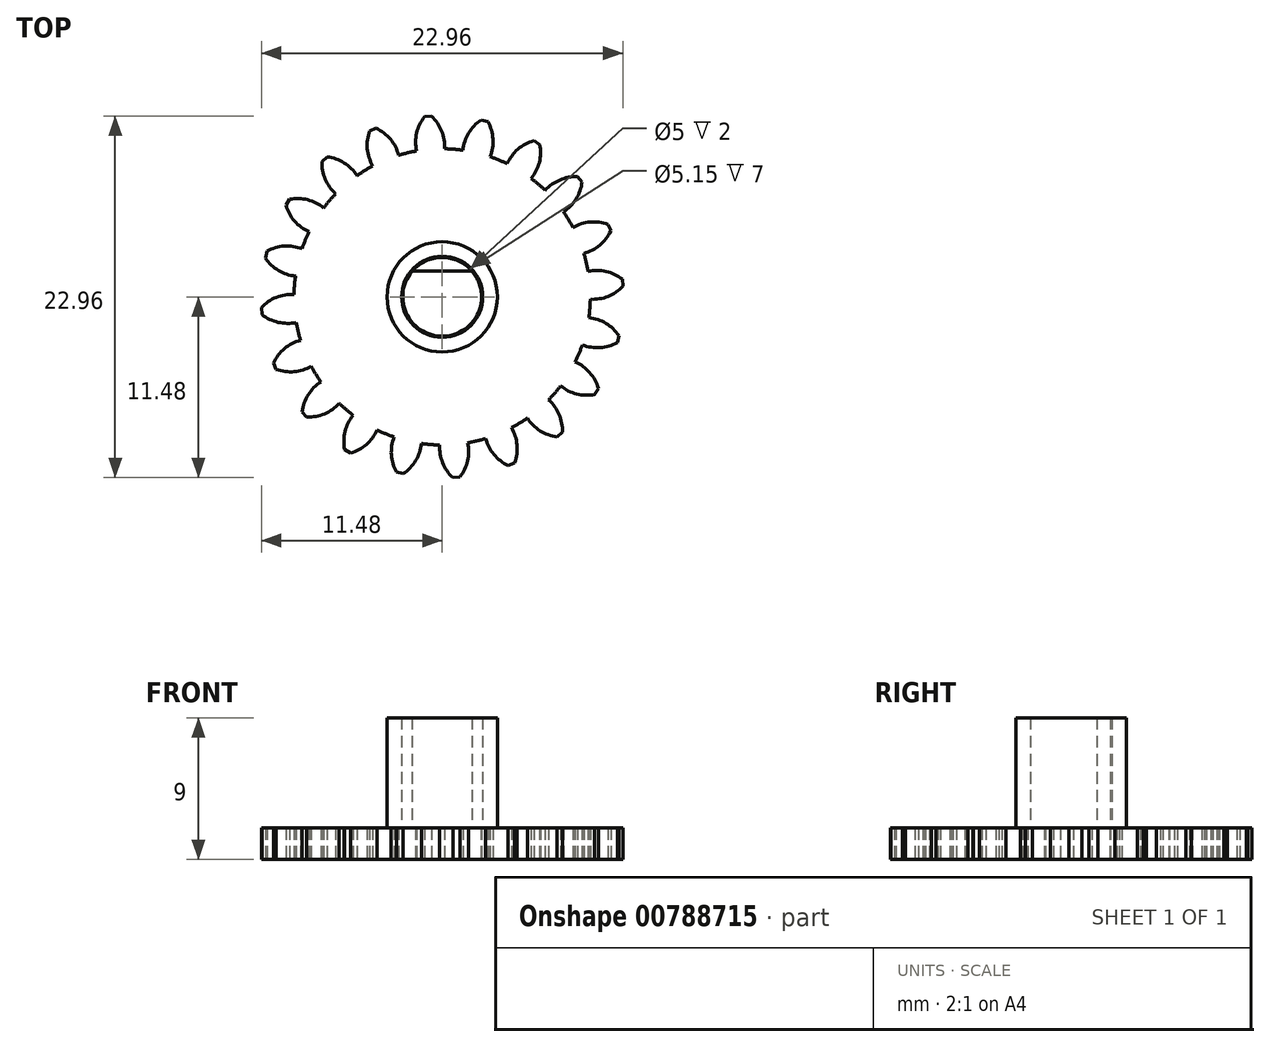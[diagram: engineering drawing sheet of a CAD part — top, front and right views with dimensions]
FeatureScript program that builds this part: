
annotation { "Feature Type Name" : "Feature", "Feature Type Description" : "" }
export const myFeature = defineFeature(function(context is Context, id is Id, definition is map)
    precondition{}
    {
        {
            assignVariable(context, id + "F0", {"name" : "GearDepth", "anyValue" : 2});
        }
        {
            var Q0;
            Q0=qCreatedBy(makeId("Top.planeOp"),FACE);
            var sketch = newSketch(context, id + "F1", { "sketchPlane" : qUnion([Q0])});
            skCircle(sketch, "E0", {"center": v(0, 0) * mm, "radius": 9.4 * mm});
            skCircle(sketch, "E1", {"center": v(0, 0) * mm, "radius": 10.45 * mm, "construction": true});
            skCircle(sketch, "E2", {"center": v(0, 0) * mm, "radius": 11.5 * mm, "construction": true});
            skLineSegment(sketch, "E3", {"start": v(0, 0) * mm, "end": v(0, 17.6) * mm, "construction": true});
            skLineSegment(sketch, "E4", {"start": v(0, 0) * mm, "end": v(-1.42, 18) * mm, "construction": true});
            skLineSegment(sketch, "E5", {"start": v(0, 10.45) * mm, "end": v(-10.54, 10.45) * mm, "construction": true});
            skLineSegment(sketch, "E6", {"start": v(0, 10.45) * mm, "end": v(-10.3, 6.7) * mm, "construction": true});
            skCircle(sketch, "E7", {"center": v(0, 10.45) * mm, "radius": 2.61 * mm, "construction": true});
            skCircle(sketch, "E8", {"center": v(-2.46, 9.56) * mm, "radius": 2.61 * mm, "construction": true});
            skArc(sketch, "E9", {"start": v(-4.91, 10.45) * mm, "mid": v(-4.92, 10.42) * mm, "end": v(-4.94, 10.39) * mm});
            skArc(sketch, "E10.trimOffspring", {"start": v(0.15, 9.4) * mm, "mid": v(-0.03, 10.54) * mm, "end": v(-0.68, 11.48) * mm});
            skArc(sketch, "E11.MirrorCS", {"start": v(-1.62, 9.27) * mm, "mid": v(-1.62, 10.41) * mm, "end": v(-1.12, 11.45) * mm});
            skLineSegment(sketch, "E12", {"start": v(-1.12, 11.45) * mm, "end": v(-0.68, 11.48) * mm});
            skArc(sketch, "E13.1.0", {"start": v(-2.76, 9) * mm, "mid": v(-3.29, 10.01) * mm, "end": v(-4.2, 10.7) * mm});
            skLineSegment(sketch, "E13.1.1", {"start": v(-4.6, 10.54) * mm, "end": v(-4.2, 10.7) * mm});
            skArc(sketch, "E13.1.2", {"start": v(-4.4, 8.31) * mm, "mid": v(-4.76, 9.4) * mm, "end": v(-4.6, 10.54) * mm});
            skArc(sketch, "E13.2.0", {"start": v(-5.4, 7.7) * mm, "mid": v(-6.22, 8.5) * mm, "end": v(-7.3, 8.89) * mm});
            skLineSegment(sketch, "E13.2.1", {"start": v(-7.64, 8.6) * mm, "end": v(-7.3, 8.89) * mm});
            skArc(sketch, "E13.2.2", {"start": v(-6.76, 6.54) * mm, "mid": v(-7.43, 7.47) * mm, "end": v(-7.64, 8.6) * mm});
            skArc(sketch, "E13.3.0", {"start": v(-7.52, 5.65) * mm, "mid": v(-8.54, 6.17) * mm, "end": v(-9.69, 6.2) * mm});
            skLineSegment(sketch, "E13.3.1", {"start": v(-9.92, 5.82) * mm, "end": v(-9.69, 6.2) * mm});
            skArc(sketch, "E13.3.2", {"start": v(-8.45, 4.13) * mm, "mid": v(-9.37, 4.81) * mm, "end": v(-9.92, 5.82) * mm});
            skArc(sketch, "E13.4.0", {"start": v(-8.9, 3.05) * mm, "mid": v(-10.03, 3.23) * mm, "end": v(-11.13, 2.9) * mm});
            skLineSegment(sketch, "E13.4.1", {"start": v(-11.23, 2.47) * mm, "end": v(-11.13, 2.9) * mm});
            skArc(sketch, "E13.4.2", {"start": v(-9.32, 1.32) * mm, "mid": v(-10.4, 1.68) * mm, "end": v(-11.23, 2.47) * mm});
            skArc(sketch, "E13.5.0", {"start": v(-9.4, 0.15) * mm, "mid": v(-10.54, -0.03) * mm, "end": v(-11.48, -0.68) * mm});
            skLineSegment(sketch, "E13.5.1", {"start": v(-11.45, -1.12) * mm, "end": v(-11.48, -0.68) * mm});
            skArc(sketch, "E13.5.2", {"start": v(-9.27, -1.62) * mm, "mid": v(-10.41, -1.62) * mm, "end": v(-11.45, -1.12) * mm});
            skArc(sketch, "E13.6.0", {"start": v(-9, -2.76) * mm, "mid": v(-10.01, -3.29) * mm, "end": v(-10.7, -4.2) * mm});
            skLineSegment(sketch, "E13.6.1", {"start": v(-10.54, -4.6) * mm, "end": v(-10.7, -4.2) * mm});
            skArc(sketch, "E13.6.2", {"start": v(-8.31, -4.4) * mm, "mid": v(-9.4, -4.76) * mm, "end": v(-10.54, -4.6) * mm});
            skArc(sketch, "E13.7.0", {"start": v(-7.7, -5.4) * mm, "mid": v(-8.5, -6.22) * mm, "end": v(-8.89, -7.3) * mm});
            skLineSegment(sketch, "E13.7.1", {"start": v(-8.6, -7.64) * mm, "end": v(-8.89, -7.3) * mm});
            skArc(sketch, "E13.7.2", {"start": v(-6.54, -6.76) * mm, "mid": v(-7.47, -7.43) * mm, "end": v(-8.6, -7.64) * mm});
            skArc(sketch, "E13.8.0", {"start": v(-5.65, -7.52) * mm, "mid": v(-6.17, -8.54) * mm, "end": v(-6.2, -9.69) * mm});
            skLineSegment(sketch, "E13.8.1", {"start": v(-5.82, -9.92) * mm, "end": v(-6.2, -9.69) * mm});
            skArc(sketch, "E13.8.2", {"start": v(-4.13, -8.45) * mm, "mid": v(-4.81, -9.37) * mm, "end": v(-5.82, -9.92) * mm});
            skArc(sketch, "E13.9.0", {"start": v(-3.05, -8.9) * mm, "mid": v(-3.23, -10.03) * mm, "end": v(-2.9, -11.13) * mm});
            skLineSegment(sketch, "E13.9.1", {"start": v(-2.47, -11.23) * mm, "end": v(-2.9, -11.13) * mm});
            skArc(sketch, "E13.9.2", {"start": v(-1.32, -9.32) * mm, "mid": v(-1.68, -10.4) * mm, "end": v(-2.47, -11.23) * mm});
            skArc(sketch, "E13.10.0", {"start": v(-0.15, -9.4) * mm, "mid": v(0.03, -10.54) * mm, "end": v(0.68, -11.48) * mm});
            skLineSegment(sketch, "E13.10.1", {"start": v(1.12, -11.45) * mm, "end": v(0.68, -11.48) * mm});
            skArc(sketch, "E13.10.2", {"start": v(1.62, -9.27) * mm, "mid": v(1.62, -10.41) * mm, "end": v(1.12, -11.45) * mm});
            skArc(sketch, "E13.11.0", {"start": v(2.76, -9) * mm, "mid": v(3.29, -10.01) * mm, "end": v(4.2, -10.7) * mm});
            skLineSegment(sketch, "E13.11.1", {"start": v(4.6, -10.54) * mm, "end": v(4.2, -10.7) * mm});
            skArc(sketch, "E13.11.2", {"start": v(4.4, -8.31) * mm, "mid": v(4.76, -9.4) * mm, "end": v(4.6, -10.54) * mm});
            skArc(sketch, "E13.12.0", {"start": v(5.4, -7.7) * mm, "mid": v(6.22, -8.5) * mm, "end": v(7.3, -8.89) * mm});
            skLineSegment(sketch, "E13.12.1", {"start": v(7.64, -8.6) * mm, "end": v(7.3, -8.89) * mm});
            skArc(sketch, "E13.12.2", {"start": v(6.76, -6.54) * mm, "mid": v(7.43, -7.47) * mm, "end": v(7.64, -8.6) * mm});
            skArc(sketch, "E13.13.0", {"start": v(7.52, -5.65) * mm, "mid": v(8.54, -6.17) * mm, "end": v(9.69, -6.2) * mm});
            skLineSegment(sketch, "E13.13.1", {"start": v(9.92, -5.82) * mm, "end": v(9.69, -6.2) * mm});
            skArc(sketch, "E13.13.2", {"start": v(8.45, -4.13) * mm, "mid": v(9.37, -4.81) * mm, "end": v(9.92, -5.82) * mm});
            skArc(sketch, "E13.14.0", {"start": v(8.9, -3.05) * mm, "mid": v(10.03, -3.23) * mm, "end": v(11.13, -2.9) * mm});
            skLineSegment(sketch, "E13.14.1", {"start": v(11.23, -2.47) * mm, "end": v(11.13, -2.9) * mm});
            skArc(sketch, "E13.14.2", {"start": v(9.32, -1.32) * mm, "mid": v(10.4, -1.68) * mm, "end": v(11.23, -2.47) * mm});
            skArc(sketch, "E13.15.0", {"start": v(9.4, -0.15) * mm, "mid": v(10.54, 0.03) * mm, "end": v(11.48, 0.68) * mm});
            skLineSegment(sketch, "E13.15.1", {"start": v(11.45, 1.12) * mm, "end": v(11.48, 0.68) * mm});
            skArc(sketch, "E13.15.2", {"start": v(9.27, 1.62) * mm, "mid": v(10.41, 1.62) * mm, "end": v(11.45, 1.12) * mm});
            skArc(sketch, "E13.16.0", {"start": v(9, 2.76) * mm, "mid": v(10.01, 3.29) * mm, "end": v(10.7, 4.2) * mm});
            skLineSegment(sketch, "E13.16.1", {"start": v(10.54, 4.6) * mm, "end": v(10.7, 4.2) * mm});
            skArc(sketch, "E13.16.2", {"start": v(8.31, 4.4) * mm, "mid": v(9.4, 4.76) * mm, "end": v(10.54, 4.6) * mm});
            skArc(sketch, "E13.17.0", {"start": v(7.7, 5.4) * mm, "mid": v(8.5, 6.22) * mm, "end": v(8.89, 7.3) * mm});
            skLineSegment(sketch, "E13.17.1", {"start": v(8.6, 7.64) * mm, "end": v(8.89, 7.3) * mm});
            skArc(sketch, "E13.17.2", {"start": v(6.54, 6.76) * mm, "mid": v(7.47, 7.43) * mm, "end": v(8.6, 7.64) * mm});
            skArc(sketch, "E13.18.0", {"start": v(5.65, 7.52) * mm, "mid": v(6.17, 8.54) * mm, "end": v(6.2, 9.69) * mm});
            skLineSegment(sketch, "E13.18.1", {"start": v(5.82, 9.92) * mm, "end": v(6.2, 9.69) * mm});
            skArc(sketch, "E13.18.2", {"start": v(4.13, 8.45) * mm, "mid": v(4.81, 9.37) * mm, "end": v(5.82, 9.92) * mm});
            skArc(sketch, "E13.19.0", {"start": v(3.05, 8.9) * mm, "mid": v(3.23, 10.03) * mm, "end": v(2.9, 11.13) * mm});
            skLineSegment(sketch, "E13.19.1", {"start": v(2.47, 11.23) * mm, "end": v(2.9, 11.13) * mm});
            skArc(sketch, "E13.19.2", {"start": v(1.32, 9.32) * mm, "mid": v(1.68, 10.4) * mm, "end": v(2.47, 11.23) * mm});
            skCircle(sketch, "E14", {"center": v(0, 0) * mm, "radius": 2.5 * mm});
            skSolve(sketch);
        }
        {
            var Q0;
            {var subQ0=sQuery(id+"F1.wireOp",EDGE,"E10.trimOffspring");Q0=makeQuery(id+"F1.imprint","IMPRINT",FACE,{"disambiguationData":[TD([[makeQuery(id+"F1.imprint","IMPRINT",EDGE,{"derivedFrom":subQ0}),1.0]])]});}
            var Q1;
            {var subQ0=sQuery(id+"F1.wireOp",EDGE,"E0");var subQ1=makeQuery(id+"F1.imprint","INTERSECT",VERTEX,{"derivedFrom":[subQ0,sQuery(id+"F1.wireOp",EDGE,"E10.trimOffspring")]});Q1=makeQuery(id+"F1.imprint","IMPRINT",FACE,{"disambiguationData":[TD([[makeQuery(id+"F1.imprint","IMPRINT",EDGE,{"disambiguationData":[TD([[subQ1,-1.0]])],"derivedFrom":subQ0}),1.0]])]});}
            var Q2;
            {var subQ0=sQuery(id+"F1.wireOp",EDGE,"E13.1.0");Q2=makeQuery(id+"F1.imprint","IMPRINT",FACE,{"disambiguationData":[TD([[makeQuery(id+"F1.imprint","IMPRINT",EDGE,{"derivedFrom":subQ0}),1.0]])]});}
            var Q3;
            {var subQ0=sQuery(id+"F1.wireOp",EDGE,"E13.2.0");Q3=makeQuery(id+"F1.imprint","IMPRINT",FACE,{"disambiguationData":[TD([[makeQuery(id+"F1.imprint","IMPRINT",EDGE,{"derivedFrom":subQ0}),1.0]])]});}
            var Q4;
            {var subQ0=sQuery(id+"F1.wireOp",EDGE,"E13.3.0");Q4=makeQuery(id+"F1.imprint","IMPRINT",FACE,{"disambiguationData":[TD([[makeQuery(id+"F1.imprint","IMPRINT",EDGE,{"derivedFrom":subQ0}),1.0]])]});}
            var Q5;
            {var subQ0=sQuery(id+"F1.wireOp",EDGE,"E13.4.0");Q5=makeQuery(id+"F1.imprint","IMPRINT",FACE,{"disambiguationData":[TD([[makeQuery(id+"F1.imprint","IMPRINT",EDGE,{"derivedFrom":subQ0}),1.0]])]});}
            var Q6;
            {var subQ0=sQuery(id+"F1.wireOp",EDGE,"E13.5.0");Q6=makeQuery(id+"F1.imprint","IMPRINT",FACE,{"disambiguationData":[TD([[makeQuery(id+"F1.imprint","IMPRINT",EDGE,{"derivedFrom":subQ0}),1.0]])]});}
            var Q7;
            {var subQ0=sQuery(id+"F1.wireOp",EDGE,"E13.6.0");Q7=makeQuery(id+"F1.imprint","IMPRINT",FACE,{"disambiguationData":[TD([[makeQuery(id+"F1.imprint","IMPRINT",EDGE,{"derivedFrom":subQ0}),1.0]])]});}
            var Q8;
            {var subQ0=sQuery(id+"F1.wireOp",EDGE,"E13.7.0");Q8=makeQuery(id+"F1.imprint","IMPRINT",FACE,{"disambiguationData":[TD([[makeQuery(id+"F1.imprint","IMPRINT",EDGE,{"derivedFrom":subQ0}),1.0]])]});}
            var Q9;
            {var subQ0=sQuery(id+"F1.wireOp",EDGE,"E13.8.0");Q9=makeQuery(id+"F1.imprint","IMPRINT",FACE,{"disambiguationData":[TD([[makeQuery(id+"F1.imprint","IMPRINT",EDGE,{"derivedFrom":subQ0}),1.0]])]});}
            var Q10;
            {var subQ0=sQuery(id+"F1.wireOp",EDGE,"E13.9.0");Q10=makeQuery(id+"F1.imprint","IMPRINT",FACE,{"disambiguationData":[TD([[makeQuery(id+"F1.imprint","IMPRINT",EDGE,{"derivedFrom":subQ0}),1.0]])]});}
            var Q11;
            {var subQ0=sQuery(id+"F1.wireOp",EDGE,"E13.10.0");Q11=makeQuery(id+"F1.imprint","IMPRINT",FACE,{"disambiguationData":[TD([[makeQuery(id+"F1.imprint","IMPRINT",EDGE,{"derivedFrom":subQ0}),1.0]])]});}
            var Q12;
            {var subQ0=sQuery(id+"F1.wireOp",EDGE,"E13.11.0");Q12=makeQuery(id+"F1.imprint","IMPRINT",FACE,{"disambiguationData":[TD([[makeQuery(id+"F1.imprint","IMPRINT",EDGE,{"derivedFrom":subQ0}),1.0]])]});}
            var Q13;
            {var subQ0=sQuery(id+"F1.wireOp",EDGE,"E13.12.0");Q13=makeQuery(id+"F1.imprint","IMPRINT",FACE,{"disambiguationData":[TD([[makeQuery(id+"F1.imprint","IMPRINT",EDGE,{"derivedFrom":subQ0}),1.0]])]});}
            var Q14;
            {var subQ0=sQuery(id+"F1.wireOp",EDGE,"E13.13.0");Q14=makeQuery(id+"F1.imprint","IMPRINT",FACE,{"disambiguationData":[TD([[makeQuery(id+"F1.imprint","IMPRINT",EDGE,{"derivedFrom":subQ0}),1.0]])]});}
            var Q15;
            {var subQ0=sQuery(id+"F1.wireOp",EDGE,"E13.14.0");Q15=makeQuery(id+"F1.imprint","IMPRINT",FACE,{"disambiguationData":[TD([[makeQuery(id+"F1.imprint","IMPRINT",EDGE,{"derivedFrom":subQ0}),1.0]])]});}
            var Q16;
            {var subQ0=sQuery(id+"F1.wireOp",EDGE,"E13.15.0");Q16=makeQuery(id+"F1.imprint","IMPRINT",FACE,{"disambiguationData":[TD([[makeQuery(id+"F1.imprint","IMPRINT",EDGE,{"derivedFrom":subQ0}),1.0]])]});}
            var Q17;
            {var subQ0=sQuery(id+"F1.wireOp",EDGE,"E13.16.0");Q17=makeQuery(id+"F1.imprint","IMPRINT",FACE,{"disambiguationData":[TD([[makeQuery(id+"F1.imprint","IMPRINT",EDGE,{"derivedFrom":subQ0}),1.0]])]});}
            var Q18;
            {var subQ0=sQuery(id+"F1.wireOp",EDGE,"E13.17.0");Q18=makeQuery(id+"F1.imprint","IMPRINT",FACE,{"disambiguationData":[TD([[makeQuery(id+"F1.imprint","IMPRINT",EDGE,{"derivedFrom":subQ0}),1.0]])]});}
            var Q19;
            {var subQ0=sQuery(id+"F1.wireOp",EDGE,"E13.18.0");Q19=makeQuery(id+"F1.imprint","IMPRINT",FACE,{"disambiguationData":[TD([[makeQuery(id+"F1.imprint","IMPRINT",EDGE,{"derivedFrom":subQ0}),1.0]])]});}
            var Q20;
            {var subQ0=sQuery(id+"F1.wireOp",EDGE,"E13.19.0");Q20=makeQuery(id+"F1.imprint","IMPRINT",FACE,{"disambiguationData":[TD([[makeQuery(id+"F1.imprint","IMPRINT",EDGE,{"derivedFrom":subQ0}),1.0]])]});}
            var Q21;
            Q21=sQuery(id+"F1.wireOp",EDGE,"E0");
            var Q22;
            Q22=sQuery(id+"F1.wireOp",EDGE,"E10.trimOffspring");
            var Q23;
            Q23=sQuery(id+"F1.wireOp",EDGE,"E12");
            var Q24;
            Q24=sQuery(id+"F1.wireOp",EDGE,"E11.MirrorCS");
            extrude(context, id + "F2", {"entities" : qUnion([Q0, Q1, Q2, Q3, Q4, Q5, Q6, Q7, Q8, Q9, Q10, Q11, Q12, Q13, Q14, Q15, Q16, Q17, Q18, Q19, Q20]), "surfaceEntities" : qUnion([Q21, Q22, Q23, Q24]), "depth" : (getVariable(context, 'GearDepth')) * mm});
        }
        {
            var Q0;
            Q0=makeQuery(id+"F2.opExtrude","CAP_FACE",FACE,{"disambiguationData":[OSD([sQuery(id+"F1.wireOp",EDGE,"E0"),sQuery(id+"F1.wireOp",EDGE,"E10.trimOffspring"),sQuery(id+"F1.wireOp",EDGE,"E11.MirrorCS"),sQuery(id+"F1.wireOp",EDGE,"E12"),sQuery(id+"F1.wireOp",EDGE,"E13.1.0"),sQuery(id+"F1.wireOp",EDGE,"E13.1.1"),sQuery(id+"F1.wireOp",EDGE,"E13.1.2"),sQuery(id+"F1.wireOp",EDGE,"E13.2.0"),sQuery(id+"F1.wireOp",EDGE,"E13.2.1"),sQuery(id+"F1.wireOp",EDGE,"E13.2.2"),sQuery(id+"F1.wireOp",EDGE,"E13.3.0"),sQuery(id+"F1.wireOp",EDGE,"E13.3.1"),sQuery(id+"F1.wireOp",EDGE,"E13.3.2"),sQuery(id+"F1.wireOp",EDGE,"E13.4.0"),sQuery(id+"F1.wireOp",EDGE,"E13.4.1"),sQuery(id+"F1.wireOp",EDGE,"E13.4.2"),sQuery(id+"F1.wireOp",EDGE,"E13.5.0"),sQuery(id+"F1.wireOp",EDGE,"E13.5.1"),sQuery(id+"F1.wireOp",EDGE,"E13.5.2"),sQuery(id+"F1.wireOp",EDGE,"E13.6.0"),sQuery(id+"F1.wireOp",EDGE,"E13.6.1"),sQuery(id+"F1.wireOp",EDGE,"E13.6.2"),sQuery(id+"F1.wireOp",EDGE,"E13.7.0"),sQuery(id+"F1.wireOp",EDGE,"E13.7.1"),sQuery(id+"F1.wireOp",EDGE,"E13.7.2"),sQuery(id+"F1.wireOp",EDGE,"E13.8.0"),sQuery(id+"F1.wireOp",EDGE,"E13.8.1"),sQuery(id+"F1.wireOp",EDGE,"E13.8.2"),sQuery(id+"F1.wireOp",EDGE,"E13.9.0"),sQuery(id+"F1.wireOp",EDGE,"E13.9.1"),sQuery(id+"F1.wireOp",EDGE,"E13.9.2"),sQuery(id+"F1.wireOp",EDGE,"E13.10.0"),sQuery(id+"F1.wireOp",EDGE,"E13.10.1"),sQuery(id+"F1.wireOp",EDGE,"E13.10.2"),sQuery(id+"F1.wireOp",EDGE,"E13.11.0"),sQuery(id+"F1.wireOp",EDGE,"E13.11.1"),sQuery(id+"F1.wireOp",EDGE,"E13.11.2"),sQuery(id+"F1.wireOp",EDGE,"E13.12.0"),sQuery(id+"F1.wireOp",EDGE,"E13.12.1"),sQuery(id+"F1.wireOp",EDGE,"E13.12.2"),sQuery(id+"F1.wireOp",EDGE,"E13.13.0"),sQuery(id+"F1.wireOp",EDGE,"E13.13.1"),sQuery(id+"F1.wireOp",EDGE,"E13.13.2"),sQuery(id+"F1.wireOp",EDGE,"E13.14.0"),sQuery(id+"F1.wireOp",EDGE,"E13.14.1"),sQuery(id+"F1.wireOp",EDGE,"E13.14.2"),sQuery(id+"F1.wireOp",EDGE,"E13.15.0"),sQuery(id+"F1.wireOp",EDGE,"E13.15.1"),sQuery(id+"F1.wireOp",EDGE,"E13.15.2"),sQuery(id+"F1.wireOp",EDGE,"E13.16.0"),sQuery(id+"F1.wireOp",EDGE,"E13.16.1"),sQuery(id+"F1.wireOp",EDGE,"E13.16.2"),sQuery(id+"F1.wireOp",EDGE,"E13.17.0"),sQuery(id+"F1.wireOp",EDGE,"E13.17.1"),sQuery(id+"F1.wireOp",EDGE,"E13.17.2"),sQuery(id+"F1.wireOp",EDGE,"E13.18.0"),sQuery(id+"F1.wireOp",EDGE,"E13.18.1"),sQuery(id+"F1.wireOp",EDGE,"E13.18.2"),sQuery(id+"F1.wireOp",EDGE,"E13.19.0"),sQuery(id+"F1.wireOp",EDGE,"E13.19.1"),sQuery(id+"F1.wireOp",EDGE,"E13.19.2"),sQuery(id+"F1.wireOp",EDGE,"E14")])],"isStart":false});
            var sketch = newSketch(context, id + "F3", { "sketchPlane" : qUnion([Q0])});
            skCircle(sketch, "E15", {"center": v(0, 0) * mm, "radius": 2.58 * mm});
            skCircle(sketch, "E16", {"center": v(0, 0) * mm, "radius": 3.5 * mm});
            skLineSegment(sketch, "E17", {"start": v(-1.9, 1.63) * mm, "end": v(1.9, 1.63) * mm});
            skSolve(sketch);
        }
        {
            var Q0;
            Q0=makeQuery(id+"F3.imprint","IMPRINT",FACE,{"disambiguationData":[TD([[makeQuery(id+"F3.imprint","IMPRINT",EDGE,{"derivedFrom":sQuery(id+"F3.wireOp",EDGE,"E16")}),1.0]])]});
            var Q1;
            {var subQ0=sQuery(id+"F3.wireOp",EDGE,"E17");Q1=makeQuery(id+"F3.imprint","IMPRINT",FACE,{"disambiguationData":[TD([[makeQuery(id+"F3.imprint","IMPRINT",EDGE,{"derivedFrom":subQ0}),1.0]])]});}
            extrude(context, id + "F4", {"entities" : qUnion([Q0, Q1]), "operationType" : NewBodyOperationType.ADD, "depth" : 7 * mm, "offsetDistance" : 25 * mm});
        }
    });
